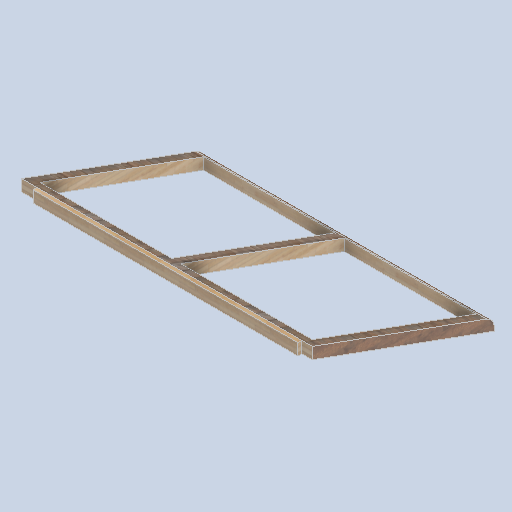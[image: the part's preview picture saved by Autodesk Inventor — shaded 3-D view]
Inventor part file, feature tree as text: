
AUTODESK INVENTOR PART (.ipt)
format: ipt  version: 2024.2 (Build 282272000, 272)  size: 172,032 bytes
history: native  units: in
note: dims shown in document units (in); Inventor stores cm internally (conversion verified against a paired STEP export)
features: sketch x6, other x3, plane x2
ambient origin geometry x8: Origin, YZ Plane, XZ Plane, XY Plane, X Axis, Y Axis, Z Axis, Center Point
bodies: Solid1 (feature_tree)
feature tree (11):
  other  "side_curve_frame_02.ipt"
  other  "Solid1::side_curve_frame_02.ipt"
  other  "TaggingFeature1"
  sketch  "Sketch1"  dims[d0=0.3937in]
  sketch  "Sketch2"
  sketch  "Sketch3"
  sketch  "Sketch4"
  sketch  "Sketch5"
  sketch  "Sketch6"
  plane  "Work Plane1"
  plane  "Work Plane2"
